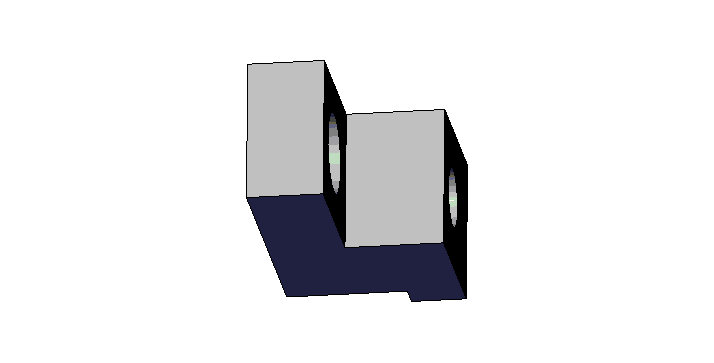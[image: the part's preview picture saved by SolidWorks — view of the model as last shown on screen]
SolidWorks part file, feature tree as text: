
SOLIDWORKS PART (.sldprt)
format: sldprt  version: not decoded by parser v0  size: 77,824 bytes
history: native  units: mm
features: plane x3, sketch x3, cut_extrude x2, extrude x1 (+7 scaffold rows collapsed)
feature tree (16):
  scaffold x7  (default folders/planes/origin — collapsed)
  plane  "Face"
  plane  "Dessus"
  plane  "Droite"
  sketch  "Esquisse2"  dims[D1=27.0mm D2=53.0mm D3=32.0mm D4=10.0mm D5=14.0mm D6=5.0mm]
  extrude  "Extrusion1"  Depth=26mm
  sketch  "Esquisse3"  dims[D1=11.0mm D2=11.0mm D3=24.0mm D4=13.0mm D5=13.5mm]
  cut_extrude  "Enlèv. mat.-Extru.1"  [1 undecoded]
  sketch  "Esquisse4"  dims[D1=15.0mm]
  cut_extrude  "Enlèv. mat.-Extru.2"  Depth=12mm
decode coverage: 5 of 6 modeling features carry decoded parameters
note: 1 parameter value undecoded
note: suppression state not decoded; provenance and decode notes live in map.json
